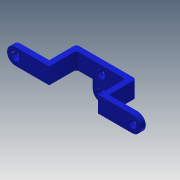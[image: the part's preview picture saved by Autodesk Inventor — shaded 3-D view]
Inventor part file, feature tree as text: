
AUTODESK INVENTOR PART (.ipt)
format: ipt  version: 2015 (Build 190159000, 159)  size: 223,744 bytes
history: native  units: mm
features: sketch x15, extrude x14, fillet x1
ambient origin geometry x8: Origin, YZ Plane, XZ Plane, XY Plane, X Axis, Y Axis, Z Axis, Center Point
bodies: Solid1 (feature_tree)
feature tree (30):
  extrude  "Extrusion1"  Depth=6.0mm
  extrude  "Extrusion2"  Depth=2.0mm
  sketch  "Sketch3"  dims[d5=2.0mm d6=10.0mm d7=0.0mm]
  extrude  "Extrusion3"  Depth=10.0mm TaperAngle=0.0deg
  extrude  "Extrusion4"  Depth=2.0mm
  sketch  "Sketch5"  dims[d10=6.0mm d11=2.0mm]
  sketch  "Sketch6"  dims[d12=14.0mm d13=0.0mm d14=14.0mm d15=0.0mm]
  extrude  "Extrusion5"  Depth=2.0mm
  extrude  "Extrusion6"  Depth=14.0mm TaperAngle=0.0deg
  extrude  "Extrusion7"  Depth=3.5mm
  extrude  "Extrusion8"  Depth=2.0mm TaperAngle=0.0deg
  fillet  "Fillet1"  Radius=3.0mm
  extrude  "Extrusion9"  Depth=3.0mm
  extrude  "Extrusion10"  Depth=1.0mm
  extrude  "Extrusion11"  Depth=3.0mm
  extrude  "Extrusion12"  Depth=6.0mm
  extrude  "Extrusion13"  Depth=3.0mm
  extrude  "Extrusion14"  Depth=2.0mm TaperAngle=0.0deg
  sketch  "Sketch15"  dims[d41=2.0mm d42=0.0mm d44=3.0mm d45=6.0mm d46=2.0mm d47=0.0mm d48=3.0mm d49=2.0mm d50=0.0mm]
  sketch  "Sketch1"  dims[d0=22.0mm d1=6.0mm]
  sketch  "Sketch2"  dims[d2=2.0mm d3=0.0mm d4=2.0mm]
  sketch  "Sketch4"  dims[d8=6.0mm d9=2.0mm]
  sketch  "Sketch7"  dims[d16=3.5mm d17=3.5mm]
  sketch  "Sketch8"  dims[d18=2.0mm d19=0.0mm d20=2.0mm d21=0.0mm d22=3.0mm]
  sketch  "Sketch9"  dims[d23=2.0mm d24=0.0mm d25=3.0mm]
  sketch  "Sketch10"  dims[d26=2.0mm d27=0.0mm d28=1.0mm]
  sketch  "Sketch11"  dims[d29=3.0mm d30=3.0mm]
  sketch  "Sketch12"  dims[d31=2.0mm d32=0.0mm d33=6.0mm]
  sketch  "Sketch13"  dims[d34=3.0mm d35=3.0mm]
  sketch  "Sketch14"  dims[d37=2.0mm d38=0.0mm d39=2.0mm d40=0.0mm]
